# Revit family: WC OPTION P_RFA
name_source: partatom
category: Aparatos sanitarios
units: mm (PartAtom-declared; Revit-internal decimal feet)

## family parameters
Activar corte en vistas = No
Compartido = No
Corte con vacíos al cargar = No
Cota de conector redondo = Usar diámetro
Mantener orientación de anotación = No
Número OmniClass = 23.45.00.00
Punto de cálculo de habitación = No
Se basa en plano de trabajo = No
Siempre vertical = Sí
Tipo de pieza = Normal
Título OmniClass = Sanitary, Laundry, and Cleaning Equipment

## types (1)
- WC Option P
    Comentarios de tipo = Ceramic
    Componentes Incluídos = Sistema de sujeción al piso.
    Descripción = Inodoro, taza tanque elongado compacto, trampa
expuesta, 4,8 LPD.
Diseño ergonómico de construcción robusta,
tecnología con sistema turvex, espejo de agua
óptimo y con trampa esmaltada.
Inodoro libre de alabeo.
    Elevación por defecto = 0"
    Fabricante = HELVEX
    High Gloss Ceramic = High Gloss Ceramic
    Imagen de tipo = <Ninguno>
    Material = Cerámica porcelanizada de alto brillo.
Calidad "A".
    Max. Working Pressure = 85.3 psi
    Maximum Consumption = 1.26 GPF
    Min. Working Pressure = 3.6 psi
    Modelo = WC Option P
    Operación = Jale la palanca para realizar la descarga.
    Total Height = 32"
    Total Length = 26"
    Total Width = 16"
    Válvulas = Válvula de admisión y descarga certificacda
Válvula de admisión silenciosa
Válvulas armadas y calibradas
Válvula de descarga con sello hermético
Válvula de descarga de Ø3" tipo sapo

## geometry (parser evidence)
native form markers: Sweep x3
no freeform markers — native parametric forms only
